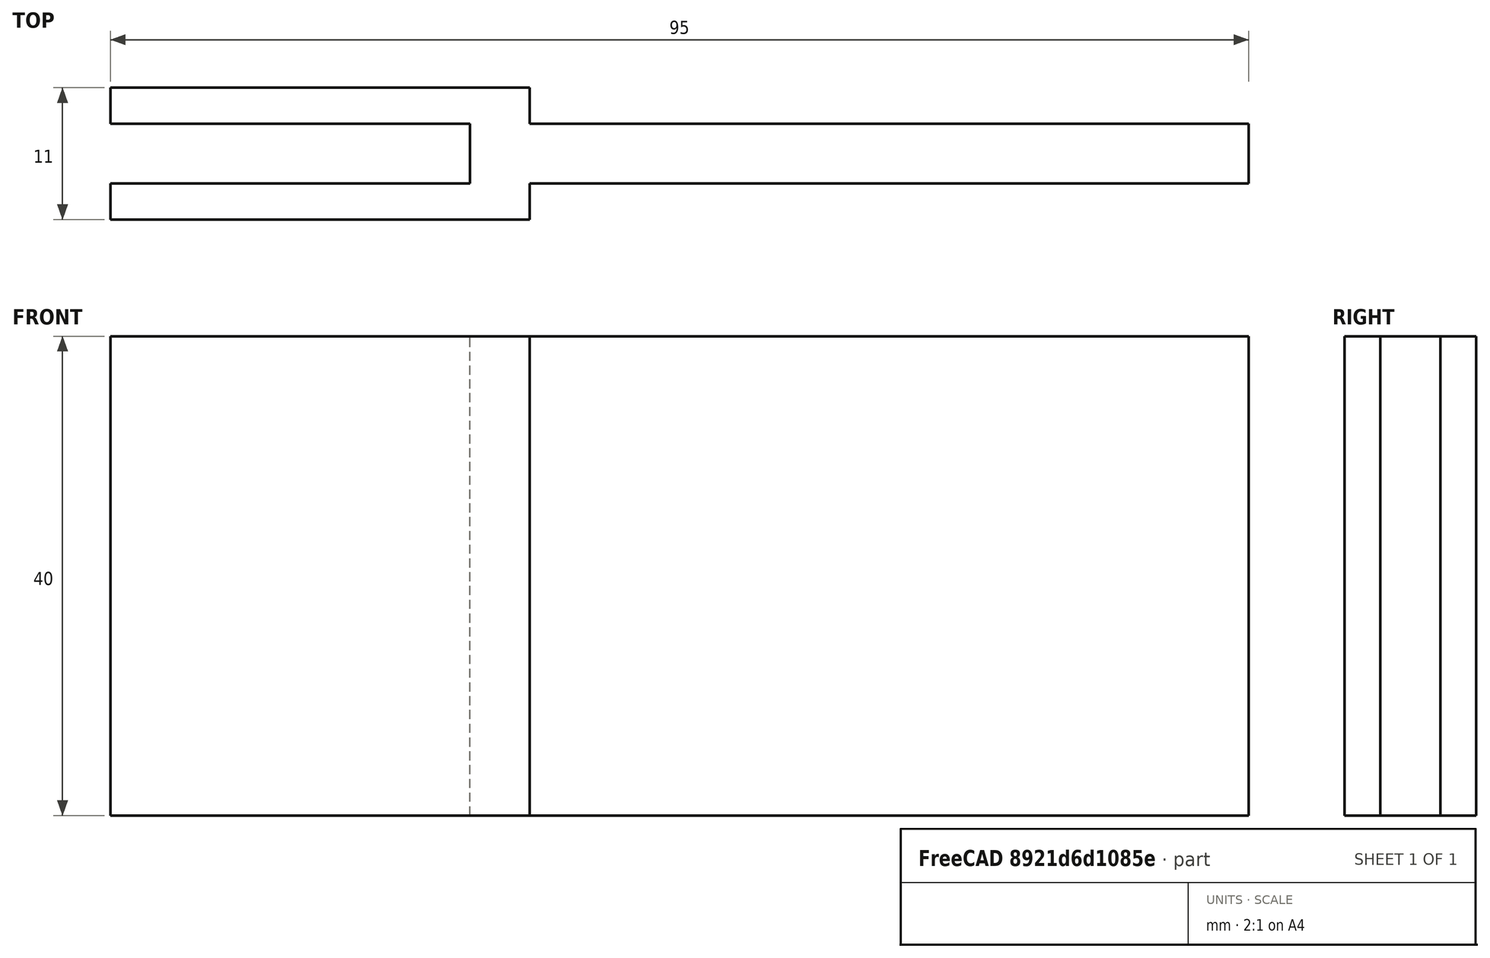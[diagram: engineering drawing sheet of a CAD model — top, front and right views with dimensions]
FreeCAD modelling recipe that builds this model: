
FCSTD DOCUMENT  (FreeCAD 0.21R33771 (Git))
Label: light-extender
License: All rights reserved
LicenseURL: https://en.wikipedia.org/wiki/All_rights_reserved
objects: Sketcher::SketchObject×1, PartDesign::Pad×1, PartDesign::Body×1
note: 4 computed .brp shape members not serialized (recipe doc carries the construction recipe); baked Part::Feature solids carry a one-line shape summary decoded from their .brp

FEATURE [Sketcher::SketchObject] Sketch
  FullyConstrained = true
  MapMode = 5
  Support = -> [XY_Plane]
  sketch-geometry (12):
    g0: LineSegment StartX=0 StartY=5.5 StartZ=0 EndX=-35 EndY=5.5 EndZ=0
    g1: LineSegment StartX=-35 StartY=5.5 StartZ=0 EndX=-35 EndY=2.5 EndZ=0
    g2: LineSegment StartX=-35 StartY=2.5 StartZ=0 EndX=-5 EndY=2.5 EndZ=0
    g3: LineSegment StartX=-5 StartY=2.5 StartZ=0 EndX=-5 EndY=-2.5 EndZ=0
    g4: LineSegment StartX=-5 StartY=-2.5 StartZ=0 EndX=-35 EndY=-2.5 EndZ=0
    g5: LineSegment StartX=-35 StartY=-2.5 StartZ=0 EndX=-35 EndY=-5.5 EndZ=0
    g6: LineSegment StartX=-35 StartY=-5.5 StartZ=0 EndX=0 EndY=-5.5 EndZ=0
    g7: LineSegment StartX=0 StartY=-5.5 StartZ=0 EndX=0 EndY=-2.5 EndZ=0
    g8: LineSegment StartX=0 StartY=-2.5 StartZ=0 EndX=60 EndY=-2.5 EndZ=0
    g9: LineSegment StartX=60 StartY=-2.5 StartZ=0 EndX=60 EndY=2.5 EndZ=0
    g10: LineSegment StartX=60 StartY=2.5 StartZ=0 EndX=0 EndY=2.5 EndZ=0
    g11: LineSegment StartX=0 StartY=2.5 StartZ=0 EndX=0 EndY=5.5 EndZ=0
  constraints (35):
    c: Horizontal(g0)
    c: Coincident(g0,g1)
    c: Coincident(g1,g2)
    c: Horizontal(g2)
    c: Coincident(g2,g3)
    c: Vertical(g3)
    c: Coincident(g3,g4)
    c: Horizontal(g4)
    c: Coincident(g4,g5)
    c: Vertical(g5)
    c: Coincident(g5,g6)
    c: Horizontal(g6)
    c: Coincident(g6,g7)
    c: Vertical(g7)
    c: Coincident(g7,g8)
    c: Horizontal(g8)
    c: Coincident(g8,g9)
    c: Vertical(g9)
    c: Coincident(g9,g10)
    c: Horizontal(g10)
    c: Coincident(g10,g11)
    c: Coincident(g11,g0)
    c: Vertical(g11)
    c: Vertical(g1)
    c: DistanceY(g3,g3) = 5
    c: DistanceY(g9,g9) = 5
    c: Horizontal(g3,g7)
    c: DistanceX(g4,g4) = 30
    c: DistanceY(g1,g1) = 3
    c: Equal(g5,g1)
    c: Vertical(g7,g10)
    c: Symmetric(g10,g7,g-1)
    c: DistanceX(g2,g10) = 5
    c: DistanceX(g8,g8) = 60
    c: Vertical(g1,g4)
FEATURE [PartDesign::Pad] Pad
  Direction = (0,0,1)
  Length = 40
  Length2 = 10
  Profile = -> Sketch
  ReferenceAxis = -> Sketch [N_Axis]
  Type = 0
FEATURE [PartDesign::Body] Body
  Group = -> [Sketch,Pad]
  Origin = -> Origin
  Tip = -> Pad
